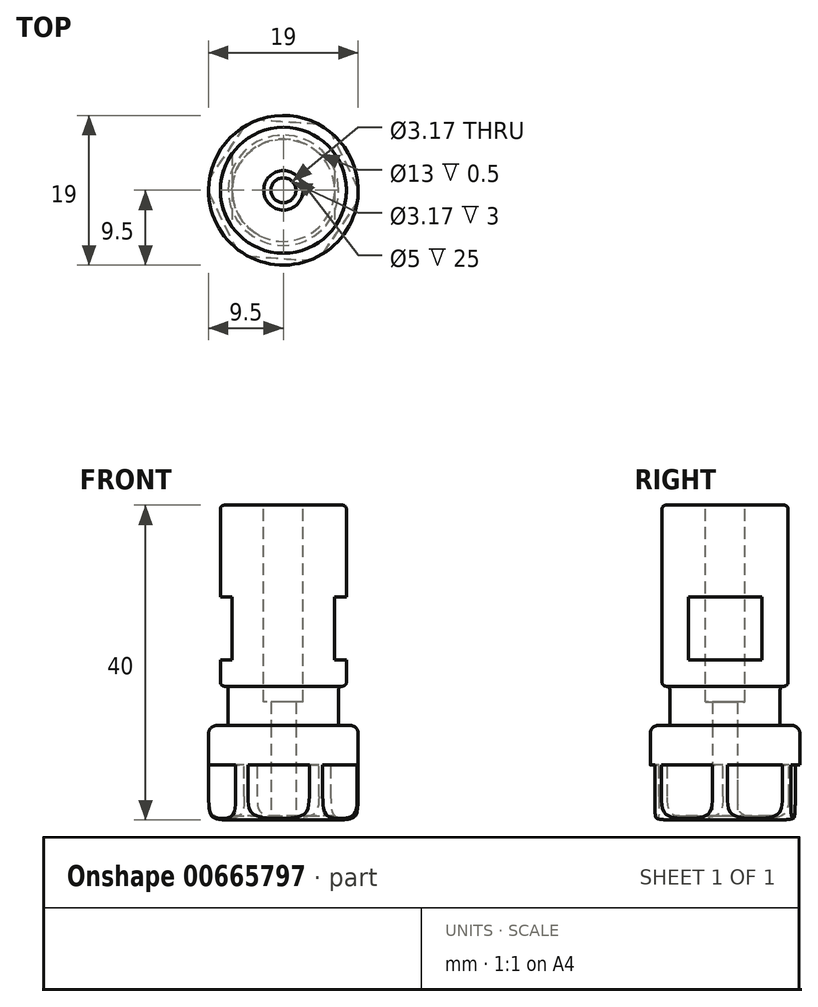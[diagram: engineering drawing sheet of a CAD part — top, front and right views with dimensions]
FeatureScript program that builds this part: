
annotation { "Feature Type Name" : "Feature", "Feature Type Description" : "" }
export const myFeature = defineFeature(function(context is Context, id is Id, definition is map)
    precondition{}
    {
        {
            var Q0;
            Q0=qCreatedBy(makeId("Top.planeOp"),FACE);
            var sketch = newSketch(context, id + "F0", { "sketchPlane" : qUnion([Q0])});
            skCircle(sketch, "E0", {"center": v(0, 0) * mm, "radius": 8 * mm});
            skSolve(sketch);
        }
        {
            var Q0;
            Q0=qSketchRegion(id+"F0",true);
            extrude(context, id + "F1", {"entities" : qUnion([Q0]), "depth" : 28 * mm, "offsetDistance" : 25 * mm});
        }
        {
            var Q0;
            Q0=qCreatedBy(makeId("Top.planeOp"),FACE);
            var sketch = newSketch(context, id + "F2", { "sketchPlane" : qUnion([Q0])});
            skCircle(sketch, "E1", {"center": v(0, 0) * mm, "radius": 7 * mm});
            skCircle(sketch, "E2", {"center": v(0, 0) * mm, "radius": 9.32 * mm});
            skSolve(sketch);
        }
        {
            var Q0;
            Q0=qSketchRegion(id+"F2",true);
            extrude(context, id + "F3", {"entities" : qUnion([Q0]), "operationType" : NewBodyOperationType.REMOVE, "depth" : 5 * mm, "offsetDistance" : 25 * mm});
        }
        {
            var Q0;
            Q0=makeQuery(id+"F1.opExtrude","CAP_FACE",FACE,{"disambiguationData":[OSD([sQuery(id+"F0.wireOp",EDGE,"E0")])],"isStart":true});
            var sketch = newSketch(context, id + "F4", { "sketchPlane" : qUnion([Q0])});
            skCircle(sketch, "E3", {"center": v(0, 0) * mm, "radius": 9.5 * mm});
            skSolve(sketch);
        }
        {
            var Q0;
            Q0=qSketchRegion(id+"F4",true);
            extrude(context, id + "F5", {"entities" : qUnion([Q0]), "depth" : 12 * mm, "offsetDistance" : 25 * mm});
        }
        {
            var Q0;
            Q0=makeQuery(id+"F5.opExtrude","CAP_FACE",FACE,{"disambiguationData":[OSD([sQuery(id+"F4.wireOp",EDGE,"E3")])],"isStart":false});
            var sketch = newSketch(context, id + "F6", { "sketchPlane" : qUnion([Q0])});
            skCircle(sketch, "E4", {"center": v(0, 0) * mm, "radius": 1.59 * mm});
            skSolve(sketch);
        }
        {
            var Q0;
            Q0=qSketchRegion(id+"F6",true);
            extrude(context, id + "F7", {"entities" : qUnion([Q0]), "operationType" : NewBodyOperationType.REMOVE, "oppositeDirection" : true, "depth" : 25 * mm, "offsetDistance" : 25 * mm});
        }
        {
            var Q0;
            Q0=makeQuery(id+"F5.opExtrude","CAP_FACE",FACE,{"disambiguationData":[OSD([sQuery(id+"F4.wireOp",EDGE,"E3")])],"isStart":false});
            var sketch = newSketch(context, id + "F8", { "sketchPlane" : qUnion([Q0])});
            skCircle(sketch, "E5.cCircle", {"center": v(0, 0) * mm, "radius": 10 * mm, "construction": true});
            skLineSegment(sketch, "E5.0", {"start": v(-5.6, 8.29) * mm, "end": v(4.38, 8.99) * mm});
            skLineSegment(sketch, "E5.1", {"start": v(4.38, 8.99) * mm, "end": v(9.98, 0.7) * mm});
            skLineSegment(sketch, "E5.2", {"start": v(9.98, 0.7) * mm, "end": v(5.6, -8.29) * mm});
            skLineSegment(sketch, "E5.3", {"start": v(5.6, -8.29) * mm, "end": v(-4.38, -8.99) * mm});
            skLineSegment(sketch, "E5.4", {"start": v(-4.38, -8.99) * mm, "end": v(-9.98, -0.7) * mm});
            skLineSegment(sketch, "E5.5", {"start": v(-9.98, -0.7) * mm, "end": v(-5.6, 8.29) * mm});
            skCircle(sketch, "E6", {"center": v(0, 0) * mm, "radius": 15.04 * mm});
            skSolve(sketch);
        }
        {
            var Q0;
            Q0=qSketchRegion(id+"F8",true);
            extrude(context, id + "F9", {"entities" : qUnion([Q0]), "operationType" : NewBodyOperationType.REMOVE, "oppositeDirection" : true, "depth" : 7 * mm, "offsetDistance" : 25 * mm});
        }
        {
            var Q0;
            Q0=makeQuery(id+"F5.opExtrude","CAP_EDGE",EDGE,{"disambiguationData":[OSD([sQuery(id+"F4.wireOp",EDGE,"E3")])],"isStart":true});
            fillet(context, id + "F10", {"entities" : qUnion([Q0]), "radius" : 1 * mm, "tangentPropagation" : true, "allowEdgeOverflow" : false});
        }
        {
            var Q0;
            {var subQ0=sQuery(id+"F4.wireOp",EDGE,"E3");Q0=makeQuery(id+"F9.boolean.opBoolean","SPLIT",EDGE,{"disambiguationData":[TD([makeQuery(id+"F5.opExtrude","SWEPT_FACE",FACE,{"disambiguationData":[OSD([subQ0])]}),makeQuery(id+"F5.opExtrude","CAP_FACE",FACE,{"disambiguationData":[OSD([subQ0])],"isStart":false}),makeQuery(id+"F9.opExtrude","SWEPT_FACE",FACE,{"disambiguationData":[OSD([sQuery(id+"F8.wireOp",EDGE,"E5.2")])]}),makeQuery(id+"F9.opExtrude","SWEPT_FACE",FACE,{"disambiguationData":[OSD([sQuery(id+"F8.wireOp",EDGE,"E5.3")])]})])],"derivedFrom":makeQuery(id+"F5.opExtrude","CAP_EDGE",EDGE,{"disambiguationData":[OSD([subQ0])],"isStart":false})});}
            fillet(context, id + "F11", {"entities" : qUnion([Q0]), "radius" : 3 * mm, "rho" : 0.7, "crossSection" : FilletCrossSection.CONIC, "allowEdgeOverflow" : false});
        }
        {
            var Q0;
            Q0=makeQuery(id+"F1.opExtrude","CAP_FACE",FACE,{"disambiguationData":[OSD([sQuery(id+"F0.wireOp",EDGE,"E0")])],"isStart":false});
            var sketch = newSketch(context, id + "F12", { "sketchPlane" : qUnion([Q0])});
            skCircle(sketch, "E7", {"center": v(0, 0) * mm, "radius": 2.5 * mm});
            skSolve(sketch);
        }
        {
            var Q0;
            Q0=qSketchRegion(id+"F12",true);
            extrude(context, id + "F13", {"entities" : qUnion([Q0]), "operationType" : NewBodyOperationType.REMOVE, "oppositeDirection" : true, "depth" : 25 * mm, "offsetDistance" : 25 * mm});
        }
        {
            var Q0;
            Q0=makeQuery(id+"F3.boolean.opBoolean","COPY",EDGE,{"derivedFrom":makeQuery(id+"F3.opExtrude","CAP_EDGE",EDGE,{"disambiguationData":[OSD([sQuery(id+"F2.wireOp",EDGE,"E1")])],"isStart":false})});
            var Q1;
            Q1=makeQuery(id+"F3.boolean.opBoolean","INTERSECT",EDGE,{"derivedFrom":[makeQuery(id+"F1.opExtrude","SWEPT_FACE",FACE,{"disambiguationData":[OSD([sQuery(id+"F0.wireOp",EDGE,"E0")])]}),makeQuery(id+"F3.opExtrude","CAP_FACE",FACE,{"disambiguationData":[OSD([sQuery(id+"F2.wireOp",EDGE,"E1"),sQuery(id+"F2.wireOp",EDGE,"E2")])],"isStart":false})]});
            var Q2;
            Q2=makeQuery(id+"F1.opExtrude","CAP_EDGE",EDGE,{"disambiguationData":[OSD([sQuery(id+"F0.wireOp",EDGE,"E0")])],"isStart":false});
            fillet(context, id + "F14", {"entities" : qUnion([Q0, Q1, Q2]), "radius" : 0.5 * mm, "tangentPropagation" : true, "allowEdgeOverflow" : false});
        }
        {
            var Q0;
            Q0=qCreatedBy(makeId("Front.planeOp"),FACE);
            var sketch = newSketch(context, id + "F15", { "sketchPlane" : qUnion([Q0])});
            skLineSegment(sketch, "E8.bottom", {"start": v(12.44, 8.34) * mm, "end": v(6.5, 8.34) * mm});
            skLineSegment(sketch, "E8.top", {"start": v(12.44, 16.34) * mm, "end": v(6.5, 16.34) * mm});
            skLineSegment(sketch, "E8.left", {"start": v(12.44, 8.34) * mm, "end": v(12.44, 16.34) * mm});
            skLineSegment(sketch, "E8.right", {"start": v(6.5, 8.34) * mm, "end": v(6.5, 16.34) * mm});
            skLineSegment(sketch, "E9", {"start": v(0, 0) * mm, "end": v(0, 36.17) * mm, "construction": true});
            skLineSegment(sketch, "E10.MirrorCS", {"start": v(-12.44, 8.34) * mm, "end": v(-6.5, 8.34) * mm});
            skLineSegment(sketch, "E11.MirrorCS", {"start": v(-12.44, 16.34) * mm, "end": v(-6.5, 16.34) * mm});
            skLineSegment(sketch, "E12.MirrorCS", {"start": v(-6.5, 8.34) * mm, "end": v(-6.5, 16.34) * mm});
            skLineSegment(sketch, "E13.MirrorCS", {"start": v(-12.44, 8.34) * mm, "end": v(-12.44, 16.34) * mm});
            skSolve(sketch);
        }
        {
            var Q0;
            Q0=qSketchRegion(id+"F15",true);
            extrude(context, id + "F16", {"entities" : qUnion([Q0]), "operationType" : NewBodyOperationType.REMOVE, "endBound" : BoundingType.SYMMETRIC, "oppositeDirection" : true, "depth" : 25 * mm, "offsetDistance" : 25 * mm});
        }
        {
            var Q0;
            Q0=makeQuery(id+"F5.opExtrude","CAP_FACE",FACE,{"disambiguationData":[OSD([sQuery(id+"F4.wireOp",EDGE,"E3")])],"isStart":false});
            extrude(context, id + "F17", {"entities" : qUnion([Q0]), "operationType" : NewBodyOperationType.REMOVE, "oppositeDirection" : true, "depth" : 0.5 * mm, "offsetDistance" : 25 * mm});
        }
    });
